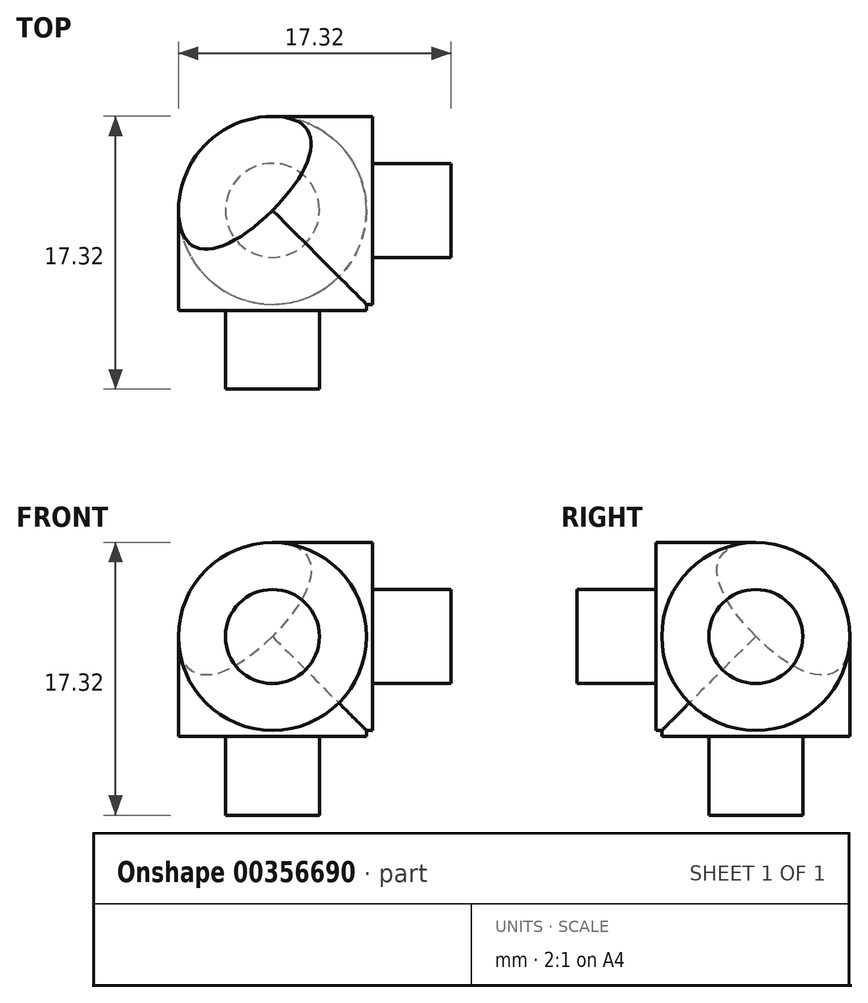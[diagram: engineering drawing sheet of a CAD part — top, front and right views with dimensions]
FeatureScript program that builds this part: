
annotation { "Feature Type Name" : "Feature", "Feature Type Description" : "" }
export const myFeature = defineFeature(function(context is Context, id is Id, definition is map)
    precondition{}
    {
        {
            var Q0;
            Q0=qCreatedBy(makeId("Top.planeOp"),FACE);
            var sketch = newSketch(context, id + "F0", { "sketchPlane" : qUnion([Q0])});
            skArc(sketch, "E0", {"start": v(0, 5.97) * mm, "mid": v(-4.22, 4.22) * mm, "end": v(-5.97, 0) * mm});
            skLineSegment(sketch, "E1", {"start": v(-5.97, 0) * mm, "end": v(-5.97, -6.35) * mm});
            skLineSegment(sketch, "E2", {"start": v(0, -6.35) * mm, "end": v(0, 0) * mm});
            skLineSegment(sketch, "E3", {"start": v(0, 0) * mm, "end": v(0, 5.97) * mm});
            skLineSegment(sketch, "E4", {"start": v(0, 0) * mm, "end": v(0, 0) * mm});
            skLineSegment(sketch, "E5", {"start": v(-2.98, -6.35) * mm, "end": v(-2.98, -11.35) * mm});
            skLineSegment(sketch, "E6", {"start": v(-2.98, -11.35) * mm, "end": v(0, -11.35) * mm});
            skLineSegment(sketch, "E7", {"start": v(0, -11.35) * mm, "end": v(0, -6.35) * mm});
            skLineSegment(sketch, "E8", {"start": v(-2.98, -6.35) * mm, "end": v(-5.97, -6.35) * mm});
            skSolve(sketch);
        }
        {
            var Q0;
            Q0=qSketchRegion(id+"F0",true);
            var Q1;
            Q1=sQuery(id+"F0.wireOp",EDGE,"E3");
            revolve(context, id + "F1", {"entities" : qUnion([Q0]), "axis" : qUnion([Q1]), "revolveType" : RevolveType.FULL});
        }
        {
            var Q0;
            Q0=qCreatedBy(makeId("Top.planeOp"),FACE);
            var sketch = newSketch(context, id + "F2", { "sketchPlane" : qUnion([Q0])});
            skLineSegment(sketch, "E9", {"start": v(-64.78, 0) * mm, "end": v(54.44, 0) * mm, "construction": true});
            skSolve(sketch);
        }
        {
            var Q0;
            Q0=makeQuery(id+"F1.opRevolve","SWEPT_BODY",BODY,{"disambiguationData":[OSD([sQuery(id+"F0.wireOp",EDGE,"E0"),sQuery(id+"F0.wireOp",EDGE,"E1"),sQuery(id+"F0.wireOp",EDGE,"q7y0TzUk-fhFp-nIsZ-NEYz-1MwVzZ4vraMZ"),sQuery(id+"F0.wireOp",EDGE,"E2"),sQuery(id+"F0.wireOp",EDGE,"E3"),sQuery(id+"F0.wireOp",EDGE,"E4")])]});
            var Q1;
            Q1=sQuery(id+"F2.wireOp",EDGE,"E9");
            circularPattern(context, id + "F3", {"entities" : qUnion([Q0]), "axis" : qUnion([Q1]), "angle" : 90 * degree, "instanceCount" : 2, "equalSpace" : true});
        }
        {
            var Q0;
            Q0=qCreatedBy(makeId("Right.planeOp"),FACE);
            var sketch = newSketch(context, id + "F4", { "sketchPlane" : qUnion([Q0])});
            skLineSegment(sketch, "E10", {"start": v(0, -52.44) * mm, "end": v(0, 42.28) * mm});
            skSolve(sketch);
        }
        {
            var Q0;
            Q0=makeQuery(id+"F1.opRevolve","SWEPT_BODY",BODY,{"disambiguationData":[OSD([sQuery(id+"F0.wireOp",EDGE,"E0"),sQuery(id+"F0.wireOp",EDGE,"E1"),sQuery(id+"F0.wireOp",EDGE,"q7y0TzUk-fhFp-nIsZ-NEYz-1MwVzZ4vraMZ"),sQuery(id+"F0.wireOp",EDGE,"E2"),sQuery(id+"F0.wireOp",EDGE,"E3"),sQuery(id+"F0.wireOp",EDGE,"E4")])]});
            var Q1;
            Q1=sQuery(id+"F4.wireOp",EDGE,"E10");
            circularPattern(context, id + "F5", {"entities" : qUnion([Q0]), "axis" : qUnion([Q1]), "angle" : 90 * degree, "instanceCount" : 2, "equalSpace" : true});
        }
        {
            var Q0;
            Q0=makeQuery(id+"F1.opRevolve","SWEPT_BODY",BODY,{"disambiguationData":[OSD([sQuery(id+"F0.wireOp",EDGE,"E0"),sQuery(id+"F0.wireOp",EDGE,"E1"),sQuery(id+"F0.wireOp",EDGE,"q7y0TzUk-fhFp-nIsZ-NEYz-1MwVzZ4vraMZ"),sQuery(id+"F0.wireOp",EDGE,"E2"),sQuery(id+"F0.wireOp",EDGE,"E3"),sQuery(id+"F0.wireOp",EDGE,"E4")])]});
            var Q1;
            Q1=makeQuery(id+"F3.opPattern","COPY",BODY,{"derivedFrom":makeQuery(id+"F1.opRevolve","SWEPT_BODY",BODY,{"disambiguationData":[OSD([sQuery(id+"F0.wireOp",EDGE,"E0"),sQuery(id+"F0.wireOp",EDGE,"E1"),sQuery(id+"F0.wireOp",EDGE,"q7y0TzUk-fhFp-nIsZ-NEYz-1MwVzZ4vraMZ"),sQuery(id+"F0.wireOp",EDGE,"E2"),sQuery(id+"F0.wireOp",EDGE,"E3"),sQuery(id+"F0.wireOp",EDGE,"E4")])]}),"instanceName":"1"});
            var Q2;
            Q2=makeQuery(id+"F5.opPattern","COPY",BODY,{"derivedFrom":makeQuery(id+"F1.opRevolve","SWEPT_BODY",BODY,{"disambiguationData":[OSD([sQuery(id+"F0.wireOp",EDGE,"E0"),sQuery(id+"F0.wireOp",EDGE,"E1"),sQuery(id+"F0.wireOp",EDGE,"q7y0TzUk-fhFp-nIsZ-NEYz-1MwVzZ4vraMZ"),sQuery(id+"F0.wireOp",EDGE,"E2"),sQuery(id+"F0.wireOp",EDGE,"E3"),sQuery(id+"F0.wireOp",EDGE,"E4")])]}),"instanceName":"1"});
            booleanBodies(context, id + "F6", {"operationType" : BooleanOperationType.UNION, "tools" : qUnion([Q0, Q1, Q2])});
        }
        {
            var Q0;
            {var subQ0=makeQuery(id+"F1.opRevolve","SWEPT_FACE",FACE,{"disambiguationData":[OSD([sQuery(id+"F0.wireOp",EDGE,"E1")])]});var subQ1=makeQuery(id+"F1.opRevolve","SWEPT_FACE",FACE,{"disambiguationData":[OSD([sQuery(id+"F0.wireOp",EDGE,"E0")])]});Q0=makeQuery(id+"F6.opBoolean","INTERSECT",VERTEX,{"derivedFrom":[subQ1,subQ0,makeQuery(id+"F3.opPattern","COPY",FACE,{"derivedFrom":subQ1,"instanceName":"1"}),makeQuery(id+"F5.opPattern","COPY",FACE,{"derivedFrom":subQ0,"instanceName":"1"})]});}
            var Q1;
            {var subQ0=makeQuery(id+"F1.opRevolve","SWEPT_FACE",FACE,{"disambiguationData":[OSD([sQuery(id+"F0.wireOp",EDGE,"E0")])]});var subQ1=makeQuery(id+"F1.opRevolve","SWEPT_FACE",FACE,{"disambiguationData":[OSD([sQuery(id+"F0.wireOp",EDGE,"E1")])]});Q1=makeQuery(id+"F6.opBoolean","INTERSECT",VERTEX,{"derivedFrom":[subQ0,subQ1,makeQuery(id+"F3.opPattern","COPY",FACE,{"derivedFrom":subQ1,"instanceName":"1"}),makeQuery(id+"F5.opPattern","COPY",FACE,{"derivedFrom":subQ0,"instanceName":"1"})]});}
            var Q2;
            {var subQ0=makeQuery(id+"F1.opRevolve","SWEPT_FACE",FACE,{"disambiguationData":[OSD([sQuery(id+"F0.wireOp",EDGE,"E1")])]});var subQ1=makeQuery(id+"F1.opRevolve","SWEPT_FACE",FACE,{"disambiguationData":[OSD([sQuery(id+"F0.wireOp",EDGE,"E0")])]});Q2=makeQuery(id+"F6.opBoolean","INTERSECT",VERTEX,{"derivedFrom":[subQ1,makeQuery(id+"F3.opPattern","COPY",FACE,{"derivedFrom":subQ1,"instanceName":"1"}),makeQuery(id+"F3.opPattern","COPY",FACE,{"derivedFrom":subQ0,"instanceName":"1"}),makeQuery(id+"F5.opPattern","COPY",FACE,{"derivedFrom":subQ1,"instanceName":"1"}),makeQuery(id+"F5.opPattern","COPY",FACE,{"derivedFrom":subQ0,"instanceName":"1"})]});}
            cPlane(context, id + "F7", {"entities" : qUnion([Q0, Q1, Q2]), "cplaneType" : CPlaneType.THREE_POINT, "offset" : 25 * mm, "width" : 150 * mm, "height" : 150 * mm});
        }
        {
            var Q0;
            Q0=qCreatedBy(id+"F7.planeOp",FACE);
            var sketch = newSketch(context, id + "F8", { "sketchPlane" : qUnion([Q0])});
            skCircle(sketch, "E11", {"center": v(0, 0) * mm, "radius": 6.63 * mm});
            skPoint(sketch, "E12.0", {"position": v(6.63, 0) * mm});
            skSolve(sketch);
        }
        {
            var Q0;
            Q0=qSketchRegion(id+"F8",true);
            extrude(context, id + "F9", {"entities" : qUnion([Q0]), "operationType" : NewBodyOperationType.REMOVE, "depth" : 25 * mm});
        }
    });
